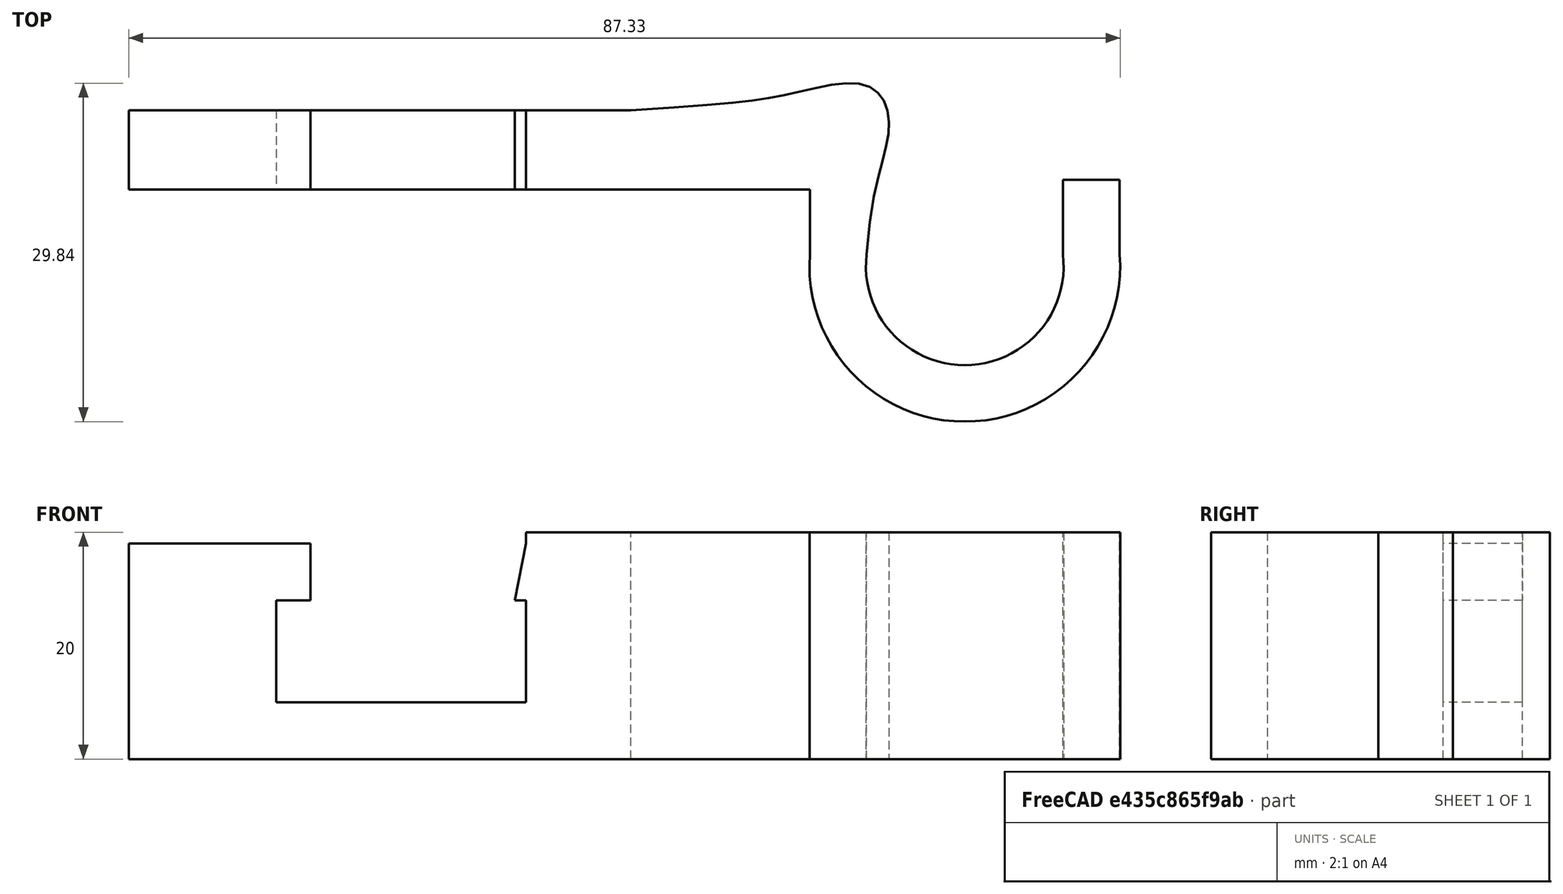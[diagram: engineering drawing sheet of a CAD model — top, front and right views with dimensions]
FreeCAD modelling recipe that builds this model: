
FCSTD DOCUMENT  (FreeCAD 0.19R24291 (Git))
Label: crochet module
License: All rights reserved
LicenseURL: http://en.wikipedia.org/wiki/All_rights_reserved
objects: TechDraw::DrawViewDimension×6, Sketcher::SketchObject×3, PartDesign::Pad×2, TechDraw::DrawViewSection×2, PartDesign::Plane×1, PartDesign::Pocket×1, PartDesign::LinearPattern×1, PartDesign::Body×1, TechDraw::DrawSVGTemplate×1, TechDraw::DrawViewPart×1, TechDraw::DrawPage×1
note: 12 computed .brp shape members not serialized (recipe doc carries the construction recipe); baked Part::Feature solids carry a one-line shape summary decoded from their .brp

FEATURE [Sketcher::SketchObject] Sketch
  FullyConstrained = false
  MapMode = 5
  Support = -> [XY_Plane]
  sketch-geometry (13):
    g0: LineSegment StartX=0 StartY=0 StartZ=0 EndX=65 EndY=0 EndZ=0
    g1: LineSegment StartX=65 StartY=0 StartZ=0 EndX=65 EndY=-12.7114 EndZ=0
    g2: LineSegment StartX=48.9999 StartY=-13.0567 StartZ=0 EndX=48.9999 EndY=-13.0567 EndZ=0
    g3: LineSegment StartX=82.2859 StartY=-12.7114 StartZ=0 EndX=82.2859 EndY=-6.13897 EndZ=0
    g4: LineSegment StartX=82.2859 StartY=-6.13897 StartZ=0 EndX=87.2859 EndY=-6.13897 EndZ=0
    g5: LineSegment StartX=87.2859 StartY=-6.13897 StartZ=0 EndX=87.2859 EndY=-12.7114 EndZ=0
    g6: LineSegment StartX=0 StartY=-7 StartZ=0 EndX=0 EndY=0 EndZ=0
    g7: LineSegment StartX=60 StartY=-12.7114 StartZ=0 EndX=60 EndY=-7 EndZ=0
    g8: LineSegment StartX=60 StartY=-7 StartZ=0 EndX=0 EndY=-7 EndZ=0
    g9: ArcOfCircle CenterX=73.643 CenterY=-13.7725 CenterZ=0 NormalX=0 NormalY=0 NormalZ=1 AngleXU=0 Radius=13.6842 StartAngle=3.06398 EndAngle=6.3608
    g10: ArcOfCircle CenterX=73.643 CenterY=-13.7725 CenterZ=0 NormalX=0 NormalY=0 NormalZ=1 AngleXU=0 Radius=8.70784 StartAngle=3.01944 EndAngle=6.40534
    g11: LineSegment StartX=28.0235 StartY=-12.7114 StartZ=0 EndX=79.2703 EndY=-12.7114 EndZ=0
    g12: LineSegment StartX=35 StartY=10.6258 StartZ=0 EndX=35 EndY=-56.7623 EndZ=0
  constraints (29):
    c: Coincident(g-1,g0)
    c: Horizontal(g0)
    c: Vertical(g1)
    c: Vertical(g3)
    c: Coincident(g3,g4)
    c: Horizontal(g4)
    c: Coincident(g4,g5)
    c: Vertical(g5)
    c: Coincident(g6,g0)
    c: Vertical(g6)
    c: Vertical(g7)
    c: Coincident(g7,g8)
    c: Horizontal(g8)
    c: Coincident(g6,g8)
    c: DistanceX(g7,g0) = 5
    c: DistanceX(g4,g4) = 5
    c: DistanceY(g6,g0) = 7
    c: Coincident(g9,g7)
    c: Coincident(g9,g5)
    c: Coincident(g10,g1)
    c: Coincident(g10,g3)
    c: Coincident(g9,g10)
    c: Horizontal(g11)
    c: PointOnObject(g7,g11)
    c: PointOnObject(g1,g11)
    c: PointOnObject(g3,g11)
    c: Vertical(g12)
    c: DistanceX(g0,g7) = 60
    c: DistanceX(g12,g7) = 25
FEATURE [PartDesign::Pad] Pad
  AllowMultiFace = false
  Direction = (1,1,1)
  Length = 20
  Length2 = 100
  Profile = -> Sketch
  Type = 0
FEATURE [PartDesign::Plane] DatumPlane
  Length = 60
  MapMode = 5
  Placement = pos=(0,0,0) rot=(0,0.707107,0.707107;3.14159rad)
  ResizeMode = 0
  Support = -> [Pad]
  Width = 60
FEATURE [Sketcher::SketchObject] Sketch001
  ExternalGeometry = -> [Sketch]
  FullyConstrained = false
  MapMode = 5
  Placement = pos=(0,0,0) rot=(0,0.707107,0.707107;3.14159rad)
  Support = -> [DatumPlane]
  sketch-geometry (17):
    g0: LineSegment StartX=0 StartY=24.034 StartZ=0 EndX=-35 EndY=24.034 EndZ=0
    g1: LineSegment StartX=-35 StartY=24.034 StartZ=0 EndX=-35 EndY=19 EndZ=0
    g2: LineSegment StartX=-35 StartY=5 StartZ=0 EndX=-13 EndY=5 EndZ=0
    g3: LineSegment StartX=-13 StartY=5 StartZ=0 EndX=-13 EndY=14 EndZ=0
    g4: LineSegment StartX=-13 StartY=14 StartZ=0 EndX=-16 EndY=14 EndZ=0
    g5: LineSegment StartX=-16 StartY=19 StartZ=0 EndX=0 EndY=19 EndZ=0
    g6: LineSegment StartX=0 StartY=19 StartZ=0 EndX=0 EndY=24.034 EndZ=0
    g7: LineSegment StartX=-60 StartY=44.1268 StartZ=0 EndX=-60 EndY=-11.5029 EndZ=0
    g8: GeomPoint X=-16 Y=19 Z=0
    g9: LineSegment StartX=-16 StartY=19 StartZ=0 EndX=-16 EndY=14 EndZ=0
    g10: LineSegment StartX=-86.6757 StartY=14 StartZ=0 EndX=33.3497 EndY=14 EndZ=0
    g11: GeomPoint X=-35 Y=14 Z=0
    g12: LineSegment StartX=-84.428 StartY=19 StartZ=0 EndX=38.0698 EndY=19 EndZ=0
    g13: GeomPoint X=-35 Y=19 Z=0
    g14: LineSegment StartX=-35 StartY=14 StartZ=0 EndX=-35 EndY=5 EndZ=0
    g15: LineSegment StartX=-35 StartY=19 StartZ=0 EndX=-34 EndY=14 EndZ=0
    g16: LineSegment StartX=-34 StartY=14 StartZ=0 EndX=-35 EndY=14 EndZ=0
  constraints (42):
    c: PointOnObject(g0,g-2)
    c: Horizontal(g0)
    c: Coincident(g0,g1)
    c: Vertical(g1)
    c: Coincident(g14,g2)
    c: Horizontal(g2)
    c: Coincident(g2,g3)
    c: Coincident(g3,g4)
    c: Horizontal(g4)
    c: Horizontal(g5)
    c: Coincident(g5,g6)
    c: Vertical(g6)
    c: Vertical(g3)
    c: Coincident(g6,g0)
    c: DistanceY(g-1,g2) = 5
    c: Vertical(g7)
    c: DistanceX(g7,g14) = 25
    c: DistanceX(g-3,g14) = 25
    c: Coincident(g9,g8)
    c: Coincident(g9,g4)
    c: Coincident(g9,g5)
    c: DistanceY(g3,g5) = 5
    c: DistanceY(g3,g3) = 9
    c: DistanceX(g2,g2) = 22
    c: DistanceX(g4,g4) = 3
    c: Horizontal(g10)
    c: PointOnObject(g3,g10)
    c: PointOnObject(g11,g1)
    c: PointOnObject(g11,g10)
    c: Horizontal(g12)
    c: PointOnObject(g5,g12)
    c: PointOnObject(g13,g1)
    c: PointOnObject(g13,g12)
    c: PointOnObject(g1,g12)
    c: PointOnObject(g14,g10)
    c: Tangent(g1,g14)
    c: Coincident(g15,g1)
    c: PointOnObject(g15,g10)
    c: Coincident(g16,g15)
    c: Coincident(g16,g14)
    c: DistanceX(g16,g16) = 1
    c: Vertical(g9)
FEATURE [PartDesign::Pocket] Pocket
  AllowMultiFace = false
  BaseFeature = -> Pad
  Length = 5
  Length2 = 100
  Profile = -> Sketch001
  Type = 1
FEATURE [Sketcher::SketchObject] Sketch002  label="renfort"
  ExternalGeometry = -> [Sketch]
  FullyConstrained = false
  MapMode = 5
  Support = -> [XY_Plane]
  sketch-geometry (15):
    g0-g6: Circle x7 (B-spline internal-alignment scaffolding for g7; pole/knot coordinates omitted)
    g7: BSplineCurve PolesCount=7 KnotsCount=5 Degree=3 IsPeriodic=0
    g8-g12: GeomPoint x5 (B-spline internal-alignment scaffolding for g7; pole/knot coordinates omitted)
    g13: LineSegment StartX=44.2275 StartY=0 StartZ=0 EndX=62.1294 EndY=-2.22554 EndZ=0
    g14: LineSegment StartX=62.1294 StartY=-2.22554 StartZ=0 EndX=65 EndY=-12.7114 EndZ=0
  constraints (9):
    c: PointOnObject(g7,g-1)
    c: Weight(g0) = 1
    c: Equal(g0, g1-g6) x6
    c: Coincident(g7,g-3)
    c: InternalAlignment(g0-g6 -> g7) x7
    c: InternalAlignment(g8-g12 -> g7) x5
    c: Coincident(g13,g7)
    c: Coincident(g14,g13)
    c: Coincident(g14,g7)
FEATURE [PartDesign::Pad] Pad001
  BaseFeature = -> Pocket
  Direction = (1,1,1)
  Length = 20
  Length2 = 100
  Profile = -> Sketch002
  Type = 0
FEATURE [PartDesign::LinearPattern] LinearPattern
  BaseFeature = -> Pad001
  Direction = -> Z_Axis
  Length = 15
  Occurrences = 1
  Originals = -> [Pad001]
FEATURE [PartDesign::Body] Body
  Group = -> [Sketch,Pad,DatumPlane,Sketch001,Pocket,Sketch002,Pad001,LinearPattern]
  Origin = -> Origin
  Tip = -> LinearPattern
FEATURE [TechDraw::DrawSVGTemplate] Template
  EditableTexts = Designed_by_Name=Designed by Name; Drawing_number=Drawing number; FC-Date=Date; FC-SC=Scale; FC-SH=Sheet; FC-Title=Title; Subtitle=Subtitle; Weight=Weight
  Height = 210
  Orientation = 1
  Width = 297
FEATURE [TechDraw::DrawViewPart] View
  CoarseView = false
  Direction = (0,0,1)
  Focus = 100
  HardHidden = false
  IsoCount = 0
  IsoHidden = false
  IsoVisible = false
  LockPosition = false
  Perspective = false
  Rotation = 0
  ScaleType = 0
  SeamHidden = false
  SeamVisible = true
  SmoothHidden = false
  SmoothVisible = true
  Source = -> [Body]
  X = 98.0712
  XDirection = (1,0,0)
  Y = 145.703
FEATURE [TechDraw::DrawViewSection] SectionView  label="Section  - "
  BaseView = -> View
  CoarseView = false
  CutSurfaceDisplay = 2
  Direction = (0,1,0)
  FileGeomPattern = D:/Program Files/FreeCAD 0.19/data/Mod/TechDraw/PAT/FCPAT.pat
  FileHatchPattern = D:/Program Files/FreeCAD 0.19/data/Mod/TechDraw/Patterns/simple.svg
  Focus = 100
  FuseBeforeCut = false
  HardHidden = false
  HatchScale = 1
  IsoCount = 0
  IsoHidden = false
  IsoVisible = false
  LockPosition = false
  NameGeomPattern = Diamond
  Perspective = false
  Rotation = 0
  ScaleType = 0
  SeamHidden = false
  SeamVisible = true
  SectionDirection = 3
  SectionNormal = (0,1,0)
  SectionOrigin = (43.7,-2.2,0)
  SmoothHidden = false
  SmoothVisible = true
  Source = -> [Body]
  X = 101.313
  XDirection = (1,0,0)
  Y = 95.2744
FEATURE [TechDraw::DrawViewSection] SectionView001  label="Section  - 001"
  BaseView = -> View
  CoarseView = false
  CutSurfaceDisplay = 2
  Direction = (-1,0,0)
  FileGeomPattern = D:/Program Files/FreeCAD 0.19/data/Mod/TechDraw/PAT/FCPAT.pat
  FileHatchPattern = D:/Program Files/FreeCAD 0.19/data/Mod/TechDraw/Patterns/simple.svg
  Focus = 100
  FuseBeforeCut = false
  HardHidden = false
  HatchScale = 1
  IsoCount = 0
  IsoHidden = false
  IsoVisible = false
  LockPosition = false
  NameGeomPattern = Diamond
  Perspective = false
  Rotation = 0
  ScaleType = 0
  SeamHidden = false
  SeamVisible = true
  SectionDirection = 0
  SectionNormal = (-1,0,0)
  SectionOrigin = (43.7,-12.2,10)
  SmoothHidden = false
  SmoothVisible = true
  Source = -> [Body]
  X = 185.961
  XDirection = (0,0,1)
  Y = 141.021
FEATURE [TechDraw::DrawViewDimension] Dimension
  Arbitrary = false
  ArbitraryTolerances = false
  EqualTolerance = true
  FormatSpec = %.2f
  FormatSpecOverTolerance = %+.2f
  FormatSpecUnderTolerance = %+.2f
  Inverted = false
  LockPosition = false
  MeasureType = 1
  OverTolerance = 0
  References2D = -> [View]
  Rotation = 0
  ScaleType = 0
  TheoreticalExact = false
  Type = 0
  UnderTolerance = 0
  X = -13.3033
  Y = -11.5053
FEATURE [TechDraw::DrawViewDimension] Dimension001
  Arbitrary = false
  ArbitraryTolerances = false
  EqualTolerance = true
  FormatSpec = %.2f
  FormatSpecOverTolerance = %+.2f
  FormatSpecUnderTolerance = %+.2f
  Inverted = false
  LockPosition = false
  MeasureType = 1
  OverTolerance = 0
  References2D = -> [View]
  Rotation = 0
  ScaleType = 0
  TheoreticalExact = false
  Type = 2
  UnderTolerance = 0
  X = -63.8351
  Y = -3.96247
FEATURE [TechDraw::DrawViewDimension] Dimension002
  Arbitrary = false
  ArbitraryTolerances = false
  EqualTolerance = true
  FormatSpec = %.2f
  FormatSpecOverTolerance = %+.2f
  FormatSpecUnderTolerance = %+.2f
  Inverted = false
  LockPosition = false
  MeasureType = 1
  OverTolerance = 0
  References2D = -> [SectionView]
  Rotation = 0
  ScaleType = 0
  TheoreticalExact = false
  Type = 1
  UnderTolerance = 0
  X = -18.5829
  Y = 16.1664
FEATURE [TechDraw::DrawViewDimension] Dimension003
  Arbitrary = false
  ArbitraryTolerances = false
  EqualTolerance = true
  FormatSpec = %.2f
  FormatSpecOverTolerance = %+.2f
  FormatSpecUnderTolerance = %+.2f
  Inverted = false
  LockPosition = false
  MeasureType = 1
  OverTolerance = 0
  References2D = -> [SectionView]
  Rotation = 0
  ScaleType = 0
  TheoreticalExact = false
  Type = 2
  UnderTolerance = 0
  X = -54.7973
  Y = -15.7093
FEATURE [TechDraw::DrawViewDimension] Dimension004
  Arbitrary = false
  ArbitraryTolerances = false
  EqualTolerance = true
  FormatSpec = %.2f
  FormatSpecOverTolerance = %+.2f
  FormatSpecUnderTolerance = %+.2f
  Inverted = false
  LockPosition = false
  MeasureType = 1
  OverTolerance = 0
  References2D = -> [SectionView]
  Rotation = 0
  ScaleType = 0
  TheoreticalExact = false
  Type = 2
  UnderTolerance = 0
  X = -66.3565
  Y = -17.5103
FEATURE [TechDraw::DrawViewDimension] Dimension005
  Arbitrary = false
  ArbitraryTolerances = false
  EqualTolerance = true
  FormatSpec = ⌀%.2f
  FormatSpecOverTolerance = %+.2f
  FormatSpecUnderTolerance = %+.2f
  Inverted = false
  LockPosition = false
  MeasureType = 1
  OverTolerance = 0
  References2D = -> [View]
  Rotation = 0
  ScaleType = 0
  TheoreticalExact = false
  Type = 5
  UnderTolerance = 0
  X = 53.6707
  Y = 1.80103
FEATURE [TechDraw::DrawPage] Page
  KeepUpdated = true
  NextBalloonIndex = 1
  ProjectionType = 0
  Template = -> Template
  Views = -> [View,SectionView,SectionView001,Dimension,Dimension001,Dimension002,Dimension003,Dimension004,Dimension005]
